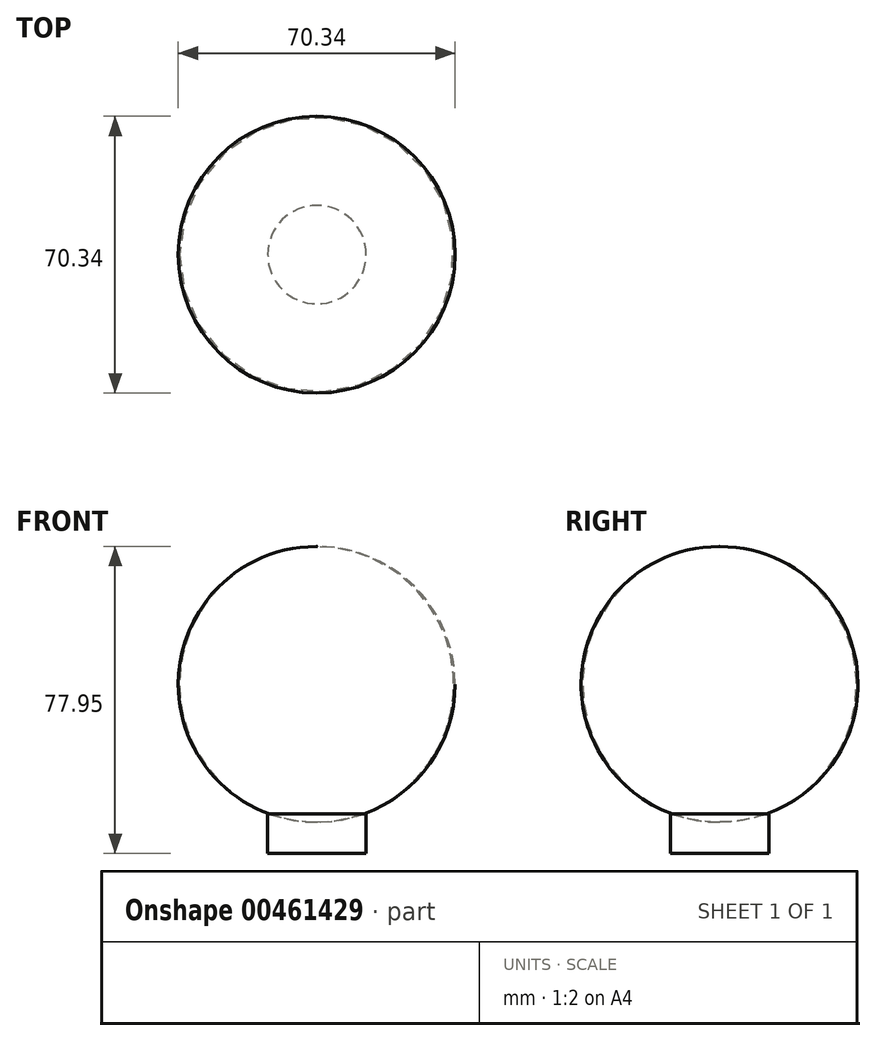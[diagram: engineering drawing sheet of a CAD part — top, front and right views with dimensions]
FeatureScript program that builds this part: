
annotation { "Feature Type Name" : "Feature", "Feature Type Description" : "" }
export const myFeature = defineFeature(function(context is Context, id is Id, definition is map)
    precondition{}
    {
        {
            var Q0;
            Q0=qCreatedBy(makeId("Front.planeOp"),FACE);
            var sketch = newSketch(context, id + "F0", { "sketchPlane" : qUnion([Q0])});
            skLineSegment(sketch, "E0", {"start": v(-14.35, 39.65) * mm, "end": v(-14.35, -30.35) * mm});
            skArc(sketch, "E1", {"start": v(-14.35, -30.35) * mm, "mid": v(20.48, 4.65) * mm, "end": v(-14.35, 39.65) * mm});
            skSolve(sketch);
        }
        {
            var Q0;
            Q0=makeQuery(id+"F0.imprint","IMPRINT",FACE,{"disambiguationData":[TD([[makeQuery(id+"F0.imprint","IMPRINT",EDGE,{"derivedFrom":sQuery(id+"F0.wireOp",EDGE,"E0")}),1.0]])]});
            var Q1;
            Q1=sQuery(id+"F0.wireOp",EDGE,"E0");
            revolve(context, id + "F1", {"entities" : qUnion([Q0]), "axis" : qUnion([Q1]), "revolveType" : RevolveType.FULL});
        }
        {
            var Q0;
            Q0=qCreatedBy(makeId("Top.planeOp"),FACE);
            cPlane(context, id + "F2", {"entities" : qUnion([Q0]), "cplaneType" : CPlaneType.OFFSET, "offset" : 28.3 * mm, "oppositeDirection" : true, "width" : 150 * mm, "height" : 150 * mm});
        }
        {
            var Q0;
            Q0=qCreatedBy(id+"F2.planeOp",FACE);
            var sketch = newSketch(context, id + "F3", { "sketchPlane" : qUnion([Q0])});
            skCircle(sketch, "E2", {"center": v(-14.28, 0) * mm, "radius": 12.5 * mm});
            skSolve(sketch);
        }
        {
            var Q0;
            Q0=makeQuery(id+"F3.imprint","IMPRINT",FACE,{"disambiguationData":[TD([[makeQuery(id+"F3.imprint","IMPRINT",EDGE,{"derivedFrom":sQuery(id+"F3.wireOp",EDGE,"E2")}),1.0]])]});
            var Q1;
            Q1=sQuery(id+"F3.wireOp",EDGE,"E2");
            extrude(context, id + "F4", {"entities" : qUnion([Q0]), "surfaceEntities" : qUnion([Q1]), "oppositeDirection" : true, "depth" : 10 * mm});
        }
    });
